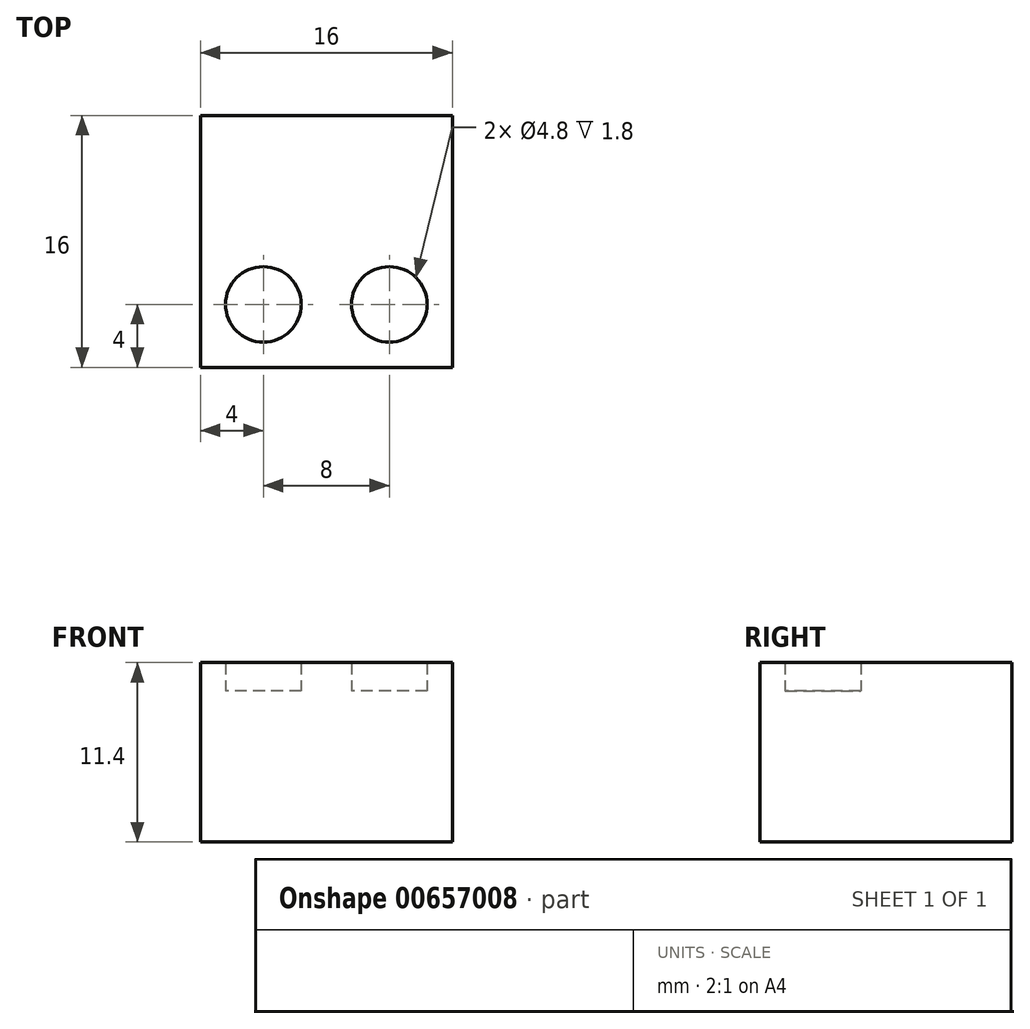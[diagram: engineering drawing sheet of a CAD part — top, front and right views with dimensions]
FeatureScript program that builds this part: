
annotation { "Feature Type Name" : "Feature", "Feature Type Description" : "" }
export const myFeature = defineFeature(function(context is Context, id is Id, definition is map)
    precondition{}
    {
        {
            var Q0;
            Q0=qCreatedBy(makeId("Top.planeOp"),FACE);
            var sketch = newSketch(context, id + "F0", { "sketchPlane" : qUnion([Q0])});
            skLineSegment(sketch, "E0.bottom", {"start": v(0, 0) * mm, "end": v(-16, 0) * mm});
            skLineSegment(sketch, "E0.top", {"start": v(0, 16) * mm, "end": v(-16, 16) * mm});
            skLineSegment(sketch, "E0.left", {"start": v(0, 0) * mm, "end": v(0, 16) * mm});
            skLineSegment(sketch, "E0.right", {"start": v(-16, 0) * mm, "end": v(-16, 16) * mm});
            skSolve(sketch);
        }
        {
            var Q0;
            Q0=makeQuery(id+"F0.imprint","IMPRINT",FACE,{"disambiguationData":[TD([[makeQuery(id+"F0.imprint","IMPRINT",EDGE,{"derivedFrom":sQuery(id+"F0.wireOp",EDGE,"E0.bottom")}),-1.0]])]});
            extrude(context, id + "F1", {"entities" : qUnion([Q0]), "depth" : 9.6 * mm, "offsetDistance" : 25.4 * mm});
        }
        {
            var Q0;
            Q0=makeQuery(id+"F1.opExtrude","CAP_FACE",FACE,{"disambiguationData":[OSD([sQuery(id+"F0.wireOp",EDGE,"E0.bottom"),sQuery(id+"F0.wireOp",EDGE,"E0.top"),sQuery(id+"F0.wireOp",EDGE,"E0.left"),sQuery(id+"F0.wireOp",EDGE,"E0.right")])],"isStart":false});
            var sketch = newSketch(context, id + "F2", { "sketchPlane" : qUnion([Q0])});
            skLineSegment(sketch, "E1", {"start": v(-16, 8) * mm, "end": v(0, 8) * mm, "construction": true});
            skLineSegment(sketch, "E2", {"start": v(-8, 16) * mm, "end": v(-8, 0) * mm, "construction": true});
            skLineSegment(sketch, "E3", {"start": v(-16, 16) * mm, "end": v(-8, 8) * mm, "construction": true});
            skLineSegment(sketch, "E4", {"start": v(-8, 8) * mm, "end": v(0, 16) * mm, "construction": true});
            skCircle(sketch, "E5", {"center": v(-12, 12) * mm, "radius": 2.4 * mm});
            skCircle(sketch, "E6", {"center": v(-4, 12) * mm, "radius": 2.4 * mm});
            skCircle(sketch, "E7.MirrorC", {"center": v(-12, 4) * mm, "radius": 2.4 * mm});
            skCircle(sketch, "E8.MirrorC", {"center": v(-4, 4) * mm, "radius": 2.4 * mm});
            skSolve(sketch);
        }
        {
            var Q0;
            Q0=makeQuery(id+"F2.imprint","IMPRINT",FACE,{"disambiguationData":[TD([[makeQuery(id+"F2.imprint","IMPRINT",EDGE,{"derivedFrom":sQuery(id+"F2.wireOp",EDGE,"E5")}),1.0]])]});
            var Q1;
            Q1=makeQuery(id+"F2.imprint","IMPRINT",FACE,{"disambiguationData":[TD([[makeQuery(id+"F2.imprint","IMPRINT",EDGE,{"derivedFrom":sQuery(id+"F2.wireOp",EDGE,"E6")}),1.0]])]});
            var Q2;
            Q2=makeQuery(id+"F2.imprint","IMPRINT",FACE,{"disambiguationData":[TD([[makeQuery(id+"F2.imprint","IMPRINT",EDGE,{"derivedFrom":sQuery(id+"F2.wireOp",EDGE,"E7.MirrorC")}),-1.0]])]});
            var Q3;
            Q3=makeQuery(id+"F2.imprint","IMPRINT",FACE,{"disambiguationData":[TD([[makeQuery(id+"F2.imprint","IMPRINT",EDGE,{"derivedFrom":sQuery(id+"F2.wireOp",EDGE,"E8.MirrorC")}),-1.0]])]});
            extrude(context, id + "F3", {"entities" : qUnion([Q0, Q1, Q2, Q3]), "operationType" : NewBodyOperationType.ADD, "depth" : 1.8 * mm, "offsetDistance" : 25.4 * mm});
        }
    });
